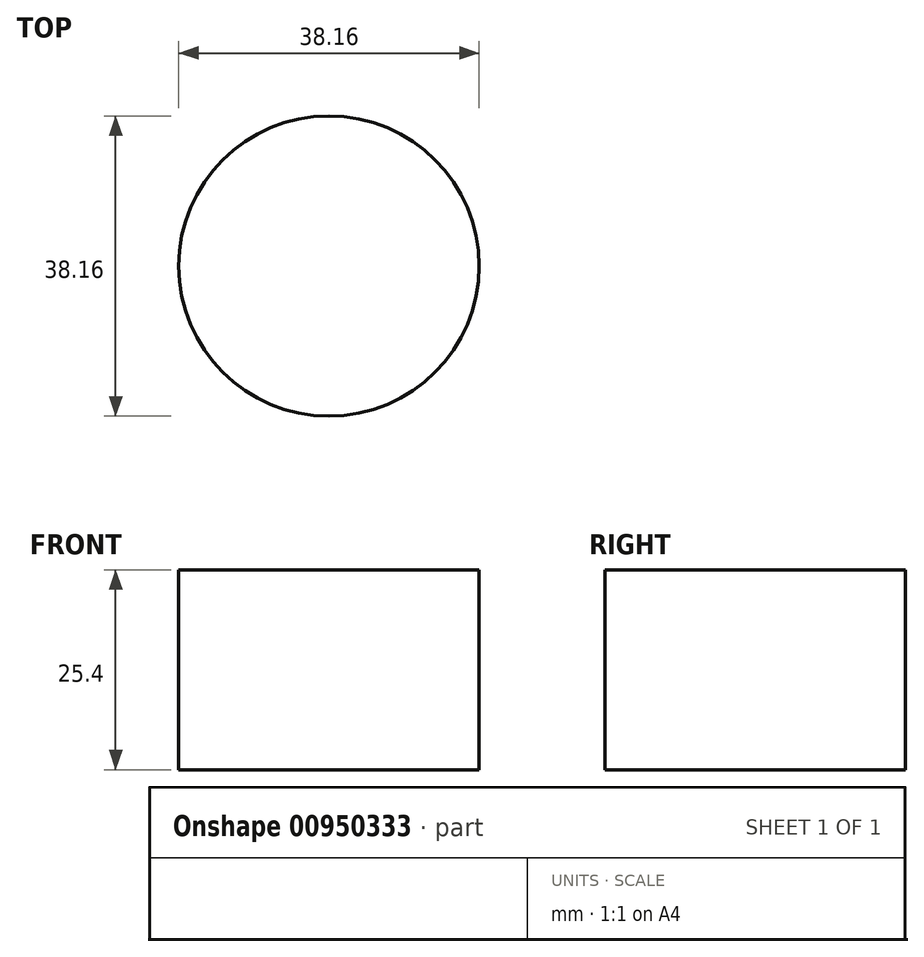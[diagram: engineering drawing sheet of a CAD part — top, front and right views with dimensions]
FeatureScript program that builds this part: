
annotation { "Feature Type Name" : "Feature", "Feature Type Description" : "" }
export const myFeature = defineFeature(function(context is Context, id is Id, definition is map)
    precondition{}
    {
        {
            var Q0;
            Q0=qCreatedBy(makeId("Top.planeOp"),FACE);
            var sketch = newSketch(context, id + "F0", { "sketchPlane" : qUnion([Q0])});
            skCircle(sketch, "E0", {"center": v(0, 0) * mm, "radius": 19.08 * mm});
            skSolve(sketch);
        }
        {
            var Q0;
            Q0=makeQuery(id+"F0.imprint","IMPRINT",FACE,{"disambiguationData":[TD([[makeQuery(id+"F0.imprint","IMPRINT",EDGE,{"derivedFrom":sQuery(id+"F0.wireOp",EDGE,"E0")}),1.0]])]});
            extrude(context, id + "F1", {"entities" : qUnion([Q0]), "depth" : 25.4 * mm, "offsetDistance" : 25.4 * mm});
        }
    });
